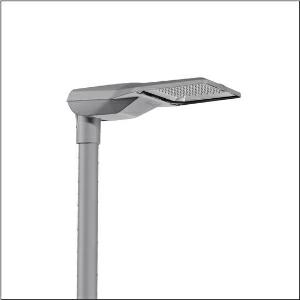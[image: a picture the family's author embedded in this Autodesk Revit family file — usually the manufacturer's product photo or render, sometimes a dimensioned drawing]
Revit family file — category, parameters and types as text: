
# Revit family: streetlight_sl_21_midi___st1_0ab_5xe7m33a08lb_7eb4
name_source: partatom
category: Lighting Fixtures
units: mm (PartAtom-declared; Revit-internal decimal feet)

## family parameters
Cut with Voids When Loaded = No
Host = Face
Light Source = No
Part Type = Normal
Room Calculation Point = No
Round Connector Dimension = Use Diameter
Shared = No

## types (1)
- --- (1 x LED, 12620 lm, 98.3 W, 3000K)
    Apparent Load = 98 VA
    CIE Flux Codes = 38 73 97 100 100
    Color Rendering = 70
    Color Temperature = 3000K
    Default Elevation = 1800 mm
    Description = Streetlight SL 21 midi, mast luminaire, primary light control with lens, of PMMA, primary optical cover: cover, of toughened safety glass, transparent, light distribution: ST1.0aB, light emission: direct distribution, primary light characteristic: asymmetric, installation type: post-top, side-entry, LED, 3G 1.5mm², High Power LED, rated luminous flux: 12.620lm, luminous efficacy: 128lm/W, light colour: 730, colour temperature: 3000K, control: flexible luminous flux parameterisation, time-dependent luminous flux control, constant luminous flux control, overheat protection, mains connection: 220..240V, AC, 50/60Hz, connection cable pre-assembled, cable length: 10,5m, wiring characteristics: H07RN-F, start of lifetime: 98W, end of service life: 101W, reduction: 44W, luminaire housing, of diecast aluminium, powder-coated, Siteco® metallic grey (DB 702S), corrosivity category C5 mid according to DIN EN ISO 12944, please order mast flange separately, inclination adjustable: 0°, 5°, 10°, 15°, sealing non-destructively replaceable, multi-level sealing system, length: 644mm, width: 335mm, height: 110mm, mast flange for spigot size: 42mm (side-entry): 5XC10008XM4, 60/48mm (side-entry/post-top): 5XC10108XM2, 76/60mm (side-entry/post-top): 5XC10108XM1, protection rating (complete): IP66, insulation class (complete): insulation class II (safety insulation), certification: CE, ENEC, ENEC+, VDE, impact resistance: IK09, permissible operating ambient temperature for outdoor applications: -40..+50°C, standard-compliant lighting for roads and squares, packaging unit: 1 piece

Light Distribution: ST1.0aB
    Height = 111 mm
    Lamp = 1 x LED
    Lamp Light Flux = 12620 lm
    Lamp Power = 98.3 W
    Lamp count = 1
    Length = 644 mm
    Luminous efficacy = 128 lm/W
    Manufacturer = Siteco
    ModVariant = No
    Model = 5XE7M33A08LB
    Number of Poles = 1
    OnlyDefault = Yes
    Power Factor = 1
    Product Name = Streetlight SL 21 midi | ST1.0aB
    Product group = mast luminaire | pylon top
    ProductGroupID = 6100
    Protection Class = Protection class II
    Protection Degree = IP 66
    RLX_Detail_Level = 1
    RLX_Emergency_Light_Flux = 0 lm
    RLX_Emergency_Type = 0
    RLX_Emergency_Type_DB = No
    RlxData = <blob elided: 90257 chars, md5=c72acc9c>
    Socket = socket
    Standby Power = 0 W
    System Light Flux = 12620 lm
    System Power = 98 W
    Type Comments = factory setting: luminous flux: 100 % | Output Level: 100 % | 1020 mA
    Type Image = l_1004298.jpg
    URL = http://relux.com
    VarID = @adj_115957
    Voltage = 0 V
    Weight = 0.00 kg
    Width = 336 mm

## geometry (parser evidence)
native form markers: Blend x4, Sweep x10
no freeform markers — native parametric forms only
